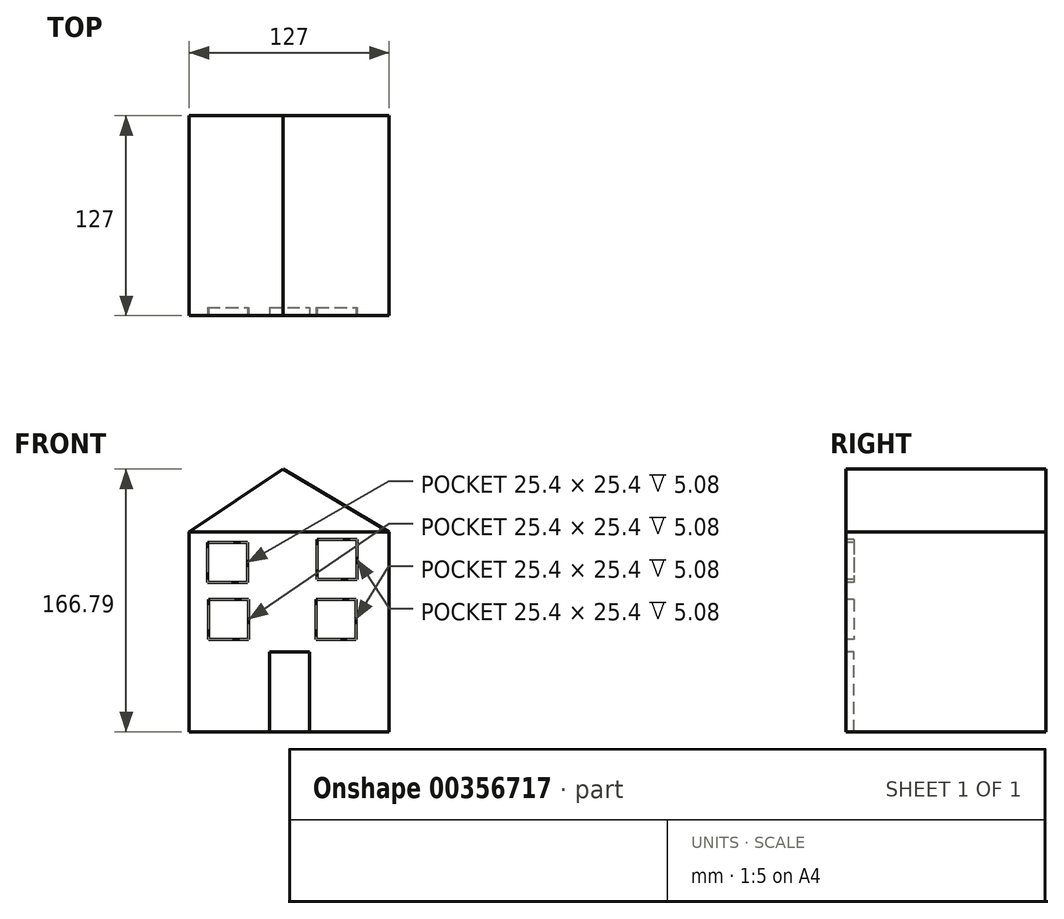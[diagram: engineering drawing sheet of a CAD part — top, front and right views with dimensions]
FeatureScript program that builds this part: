
annotation { "Feature Type Name" : "Feature", "Feature Type Description" : "" }
export const myFeature = defineFeature(function(context is Context, id is Id, definition is map)
    precondition{}
    {
        {
            var Q0;
            Q0=qCreatedBy(makeId("Front.planeOp"),FACE);
            var sketch = newSketch(context, id + "F0", { "sketchPlane" : qUnion([Q0])});
            skLineSegment(sketch, "E0.bottom", {"start": v(-50.91, 90.07) * mm, "end": v(76.09, 90.07) * mm});
            skLineSegment(sketch, "E0.top", {"start": v(-50.91, -36.93) * mm, "end": v(76.09, -36.93) * mm});
            skLineSegment(sketch, "E0.left", {"start": v(-50.91, 90.07) * mm, "end": v(-50.91, -36.93) * mm});
            skLineSegment(sketch, "E0.right", {"start": v(76.09, 90.07) * mm, "end": v(76.09, -36.93) * mm});
            skSolve(sketch);
        }
        {
            var Q0;
            Q0=makeQuery(id+"F0.imprint","IMPRINT",FACE,{"disambiguationData":[TD([[makeQuery(id+"F0.imprint","IMPRINT",EDGE,{"derivedFrom":sQuery(id+"F0.wireOp",EDGE,"E0.bottom")}),-1.0]])]});
            extrude(context, id + "F1", {"entities" : qUnion([Q0]), "depth" : 127 * mm});
        }
        {
            var Q0;
            Q0=makeQuery(id+"F1.opExtrude","CAP_FACE",FACE,{"disambiguationData":[OSD([sQuery(id+"F0.wireOp",EDGE,"E0.bottom"),sQuery(id+"F0.wireOp",EDGE,"E0.top"),sQuery(id+"F0.wireOp",EDGE,"E0.left"),sQuery(id+"F0.wireOp",EDGE,"E0.right")])],"isStart":false});
            var sketch = newSketch(context, id + "F2", { "sketchPlane" : qUnion([Q0])});
            skLineSegment(sketch, "E1.bottom", {"start": v(0, -36.93) * mm, "end": v(25.4, -36.93) * mm});
            skLineSegment(sketch, "E1.top", {"start": v(0, 13.87) * mm, "end": v(25.4, 13.87) * mm});
            skLineSegment(sketch, "E1.left", {"start": v(0, -36.93) * mm, "end": v(0, 13.87) * mm});
            skLineSegment(sketch, "E1.right", {"start": v(25.4, -36.93) * mm, "end": v(25.4, 13.87) * mm});
            skLineSegment(sketch, "E2.bottom", {"start": v(-39.25, 83.23) * mm, "end": v(-13.85, 83.23) * mm});
            skLineSegment(sketch, "E2.top", {"start": v(-39.25, 57.83) * mm, "end": v(-13.85, 57.83) * mm});
            skLineSegment(sketch, "E2.left", {"start": v(-39.25, 83.23) * mm, "end": v(-39.25, 57.83) * mm});
            skLineSegment(sketch, "E2.right", {"start": v(-13.85, 83.23) * mm, "end": v(-13.85, 57.83) * mm});
            skLineSegment(sketch, "E3.bottom", {"start": v(30.22, 85.25) * mm, "end": v(55.62, 85.25) * mm});
            skLineSegment(sketch, "E3.top", {"start": v(30.22, 59.85) * mm, "end": v(55.62, 59.85) * mm});
            skLineSegment(sketch, "E3.left", {"start": v(30.22, 85.25) * mm, "end": v(30.22, 59.85) * mm});
            skLineSegment(sketch, "E3.right", {"start": v(55.62, 85.25) * mm, "end": v(55.62, 59.85) * mm});
            skLineSegment(sketch, "E4.bottom", {"start": v(-38.75, 46.99) * mm, "end": v(-13.35, 46.99) * mm});
            skLineSegment(sketch, "E4.top", {"start": v(-38.75, 21.59) * mm, "end": v(-13.35, 21.59) * mm});
            skLineSegment(sketch, "E4.left", {"start": v(-38.75, 46.99) * mm, "end": v(-38.75, 21.59) * mm});
            skLineSegment(sketch, "E4.right", {"start": v(-13.35, 46.99) * mm, "end": v(-13.35, 21.59) * mm});
            skLineSegment(sketch, "E5.bottom", {"start": v(29.72, 46.99) * mm, "end": v(55.12, 46.99) * mm});
            skLineSegment(sketch, "E5.top", {"start": v(29.72, 21.59) * mm, "end": v(55.12, 21.59) * mm});
            skLineSegment(sketch, "E5.left", {"start": v(29.72, 46.99) * mm, "end": v(29.72, 21.59) * mm});
            skLineSegment(sketch, "E5.right", {"start": v(55.12, 46.99) * mm, "end": v(55.12, 21.59) * mm});
            skSolve(sketch);
        }
        {
            var Q0;
            Q0=makeQuery(id+"F2.imprint","IMPRINT",FACE,{"disambiguationData":[TD([[makeQuery(id+"F2.imprint","IMPRINT",EDGE,{"derivedFrom":sQuery(id+"F2.wireOp",EDGE,"E2.bottom")}),-1.0]])]});
            var Q1;
            Q1=makeQuery(id+"F2.imprint","IMPRINT",FACE,{"disambiguationData":[TD([[makeQuery(id+"F2.imprint","IMPRINT",EDGE,{"derivedFrom":sQuery(id+"F2.wireOp",EDGE,"E4.bottom")}),-1.0]])]});
            var Q2;
            Q2=makeQuery(id+"F2.imprint","IMPRINT",FACE,{"disambiguationData":[TD([[makeQuery(id+"F2.imprint","IMPRINT",EDGE,{"derivedFrom":sQuery(id+"F2.wireOp",EDGE,"E1.bottom")}),1.0]])]});
            var Q3;
            Q3=makeQuery(id+"F2.imprint","IMPRINT",FACE,{"disambiguationData":[TD([[makeQuery(id+"F2.imprint","IMPRINT",EDGE,{"derivedFrom":sQuery(id+"F2.wireOp",EDGE,"E5.bottom")}),-1.0]])]});
            var Q4;
            Q4=makeQuery(id+"F2.imprint","IMPRINT",FACE,{"disambiguationData":[TD([[makeQuery(id+"F2.imprint","IMPRINT",EDGE,{"derivedFrom":sQuery(id+"F2.wireOp",EDGE,"E3.bottom")}),-1.0]])]});
            extrude(context, id + "F3", {"entities" : qUnion([Q0, Q1, Q2, Q3, Q4]), "operationType" : NewBodyOperationType.REMOVE, "oppositeDirection" : true, "depth" : 5.08 * mm});
        }
        {
            var Q0;
            Q0=makeQuery(id+"F1.opExtrude","CAP_FACE",FACE,{"disambiguationData":[OSD([sQuery(id+"F0.wireOp",EDGE,"E0.bottom"),sQuery(id+"F0.wireOp",EDGE,"E0.top"),sQuery(id+"F0.wireOp",EDGE,"E0.left"),sQuery(id+"F0.wireOp",EDGE,"E0.right")])],"isStart":false});
            var sketch = newSketch(context, id + "F4", { "sketchPlane" : qUnion([Q0])});
            skLineSegment(sketch, "E6", {"start": v(-50.91, 90.07) * mm, "end": v(8.55, 129.86) * mm});
            skLineSegment(sketch, "E7", {"start": v(8.55, 129.86) * mm, "end": v(76.09, 90.07) * mm});
            skSolve(sketch);
        }
        {
            var Q0;
            Q0=makeQuery(id+"F4.imprint","IMPRINT",FACE,{"disambiguationData":[TD([[makeQuery(id+"F4.imprint","IMPRINT",EDGE,{"derivedFrom":sQuery(id+"F4.wireOp",EDGE,"E6")}),-1.0]])]});
            extrude(context, id + "F5", {"entities" : qUnion([Q0]), "oppositeDirection" : true, "depth" : 127 * mm});
        }
    });
